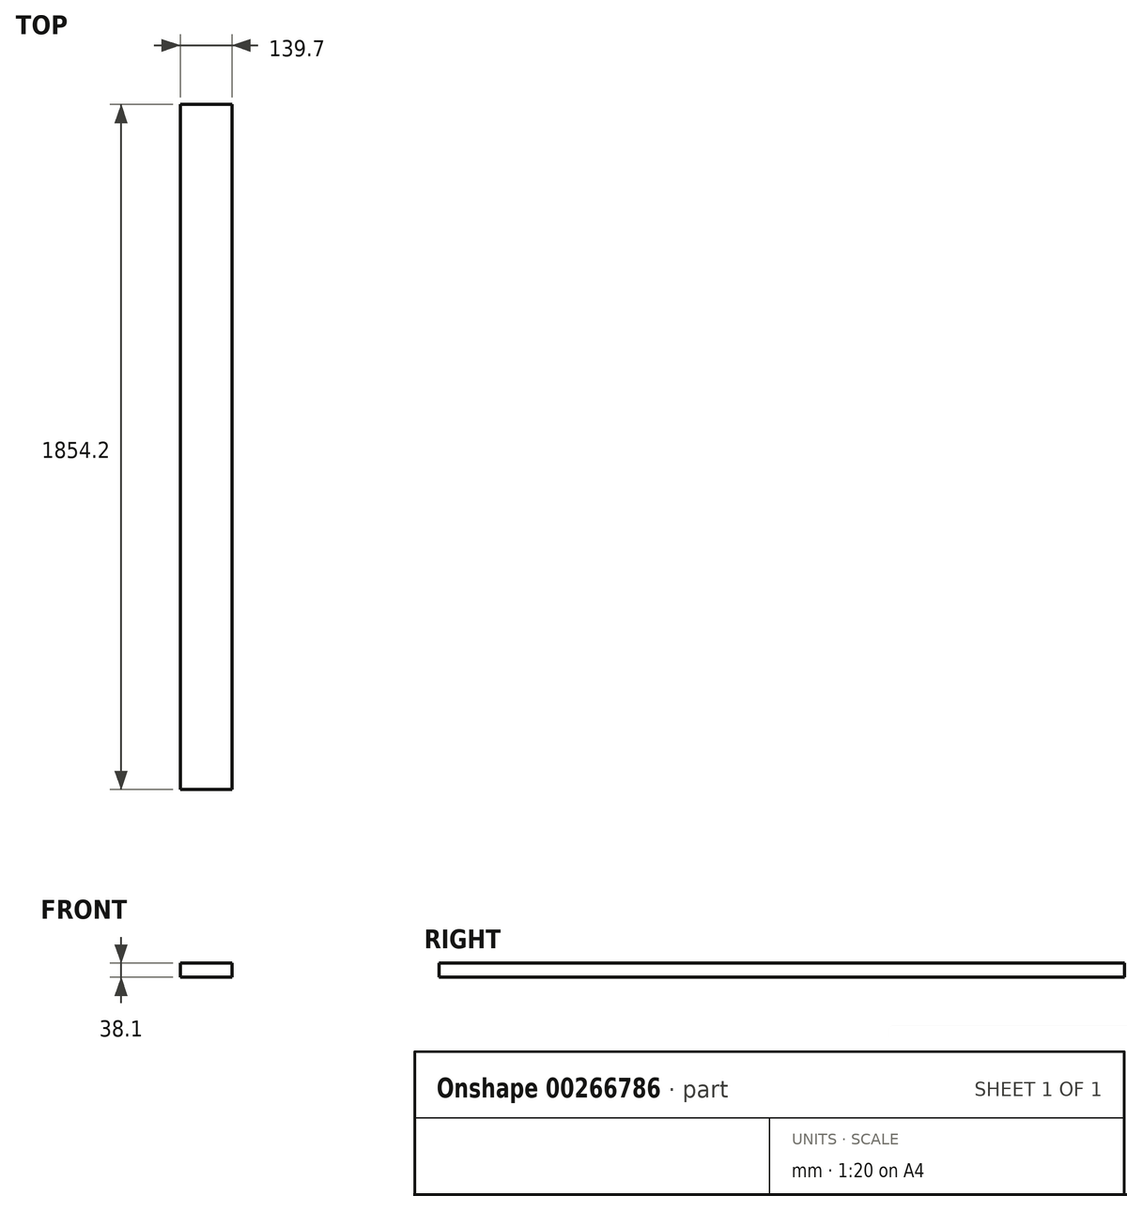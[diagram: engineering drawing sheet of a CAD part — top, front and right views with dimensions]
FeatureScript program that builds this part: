
annotation { "Feature Type Name" : "Feature", "Feature Type Description" : "" }
export const myFeature = defineFeature(function(context is Context, id is Id, definition is map)
    precondition{}
    {
        {
            var Q0;
            Q0=qCreatedBy(makeId("Front.planeOp"),FACE);
            var sketch = newSketch(context, id + "F0", { "sketchPlane" : qUnion([Q0])});
            skLineSegment(sketch, "E0.bottom", {"start": v(-48.34, 23.68) * mm, "end": v(91.36, 23.68) * mm});
            skLineSegment(sketch, "E0.top", {"start": v(-48.34, -14.42) * mm, "end": v(91.36, -14.42) * mm});
            skLineSegment(sketch, "E0.left", {"start": v(-48.34, 23.68) * mm, "end": v(-48.34, -14.42) * mm});
            skLineSegment(sketch, "E0.right", {"start": v(91.36, 23.68) * mm, "end": v(91.36, -14.42) * mm});
            skSolve(sketch);
        }
        {
            var Q0;
            Q0=qSketchRegion(id+"F0",true);
            extrude(context, id + "F1", {"entities" : qUnion([Q0]), "depth" : 1854.2 * mm});
        }
    });
